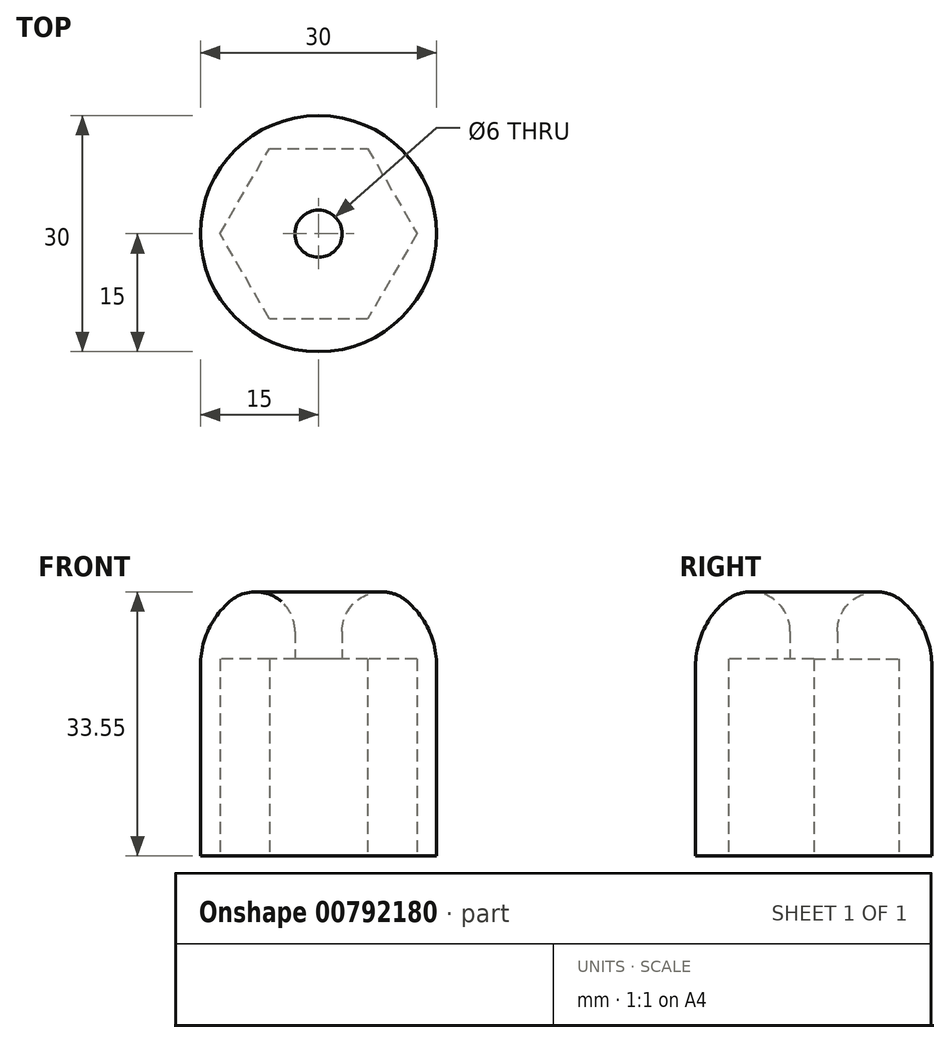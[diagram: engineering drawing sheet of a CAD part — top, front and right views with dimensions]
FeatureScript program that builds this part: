
annotation { "Feature Type Name" : "Feature", "Feature Type Description" : "" }
export const myFeature = defineFeature(function(context is Context, id is Id, definition is map)
    precondition{}
    {
        {
            var Q0;
            Q0=qCreatedBy(makeId("Top.planeOp"),FACE);
            var sketch = newSketch(context, id + "F0", { "sketchPlane" : qUnion([Q0])});
            skCircle(sketch, "E0.cCircle", {"center": v(0, 0) * mm, "radius": 12.5 * mm, "construction": true});
            skLineSegment(sketch, "E0.0", {"start": v(6.25, -10.83) * mm, "end": v(-6.25, -10.83) * mm});
            skLineSegment(sketch, "E0.1", {"start": v(-6.25, -10.83) * mm, "end": v(-12.5, 0) * mm});
            skLineSegment(sketch, "E0.2", {"start": v(-12.5, 0) * mm, "end": v(-6.25, 10.83) * mm});
            skLineSegment(sketch, "E0.3", {"start": v(-6.25, 10.83) * mm, "end": v(6.25, 10.83) * mm});
            skLineSegment(sketch, "E0.4", {"start": v(6.25, 10.83) * mm, "end": v(12.5, 0) * mm});
            skLineSegment(sketch, "E0.5", {"start": v(12.5, 0) * mm, "end": v(6.25, -10.83) * mm});
            skLineSegment(sketch, "E1", {"start": v(0, 0) * mm, "end": v(-16.89, 0) * mm, "construction": true});
            skCircle(sketch, "E2", {"center": v(0, 0) * mm, "radius": 15 * mm});
            skCircle(sketch, "E3", {"center": v(0, 0) * mm, "radius": 3 * mm});
            skSolve(sketch);
        }
        {
            var Q0;
            Q0 = qSketchRegion(id + "F0", true);
            extrude(context, id + "F1", {"entities" : qUnion([Q0]), "depth" : 25 * mm, "offsetDistance" : 25 * mm});
        }
        {
            var Q0;
            Q0=makeQuery(id+"F0.imprint","IMPRINT",FACE,{"disambiguationData":[TD([[makeQuery(id+"F0.imprint","IMPRINT",EDGE,{"derivedFrom":sQuery(id+"F0.wireOp",EDGE,"E0.0")}),1.0]])]});
            var Q1;
            Q1=makeQuery(id+"F0.imprint","IMPRINT",FACE,{"disambiguationData":[TD([[makeQuery(id+"F0.imprint","IMPRINT",EDGE,{"derivedFrom":sQuery(id+"F0.wireOp",EDGE,"E0.0")}),-1.0]])]});
            extrude(context, id + "F2", {"entities" : qUnion([Q0, Q1]), "operationType" : NewBodyOperationType.ADD, "depth" : 35 * mm, "offsetDistance" : 25 * mm, "hasSecondDirection" : true, "secondDirectionOppositeDirection" : false, "secondDirectionDepth" : 25 * mm});
        }
        {
            var Q0;
            Q0=makeQuery(id+"F2.opExtrude","CAP_EDGE",EDGE,{"disambiguationData":[OSD([sQuery(id+"F0.wireOp",EDGE,"E2")])],"isStart":false});
            fillet(context, id + "F3", {"entities" : qUnion([Q0]), "radius" : 10.86 * mm, "tangentPropagation" : true, "allowEdgeOverflow" : false});
        }
        {
            var Q0;
            Q0=makeQuery(id+"F2.opExtrude","CAP_EDGE",EDGE,{"disambiguationData":[OSD([sQuery(id+"F0.wireOp",EDGE,"E3")])],"isStart":false});
            fillet(context, id + "F4", {"entities" : qUnion([Q0]), "radius" : 5 * mm, "tangentPropagation" : true, "allowEdgeOverflow" : false});
        }
    });
